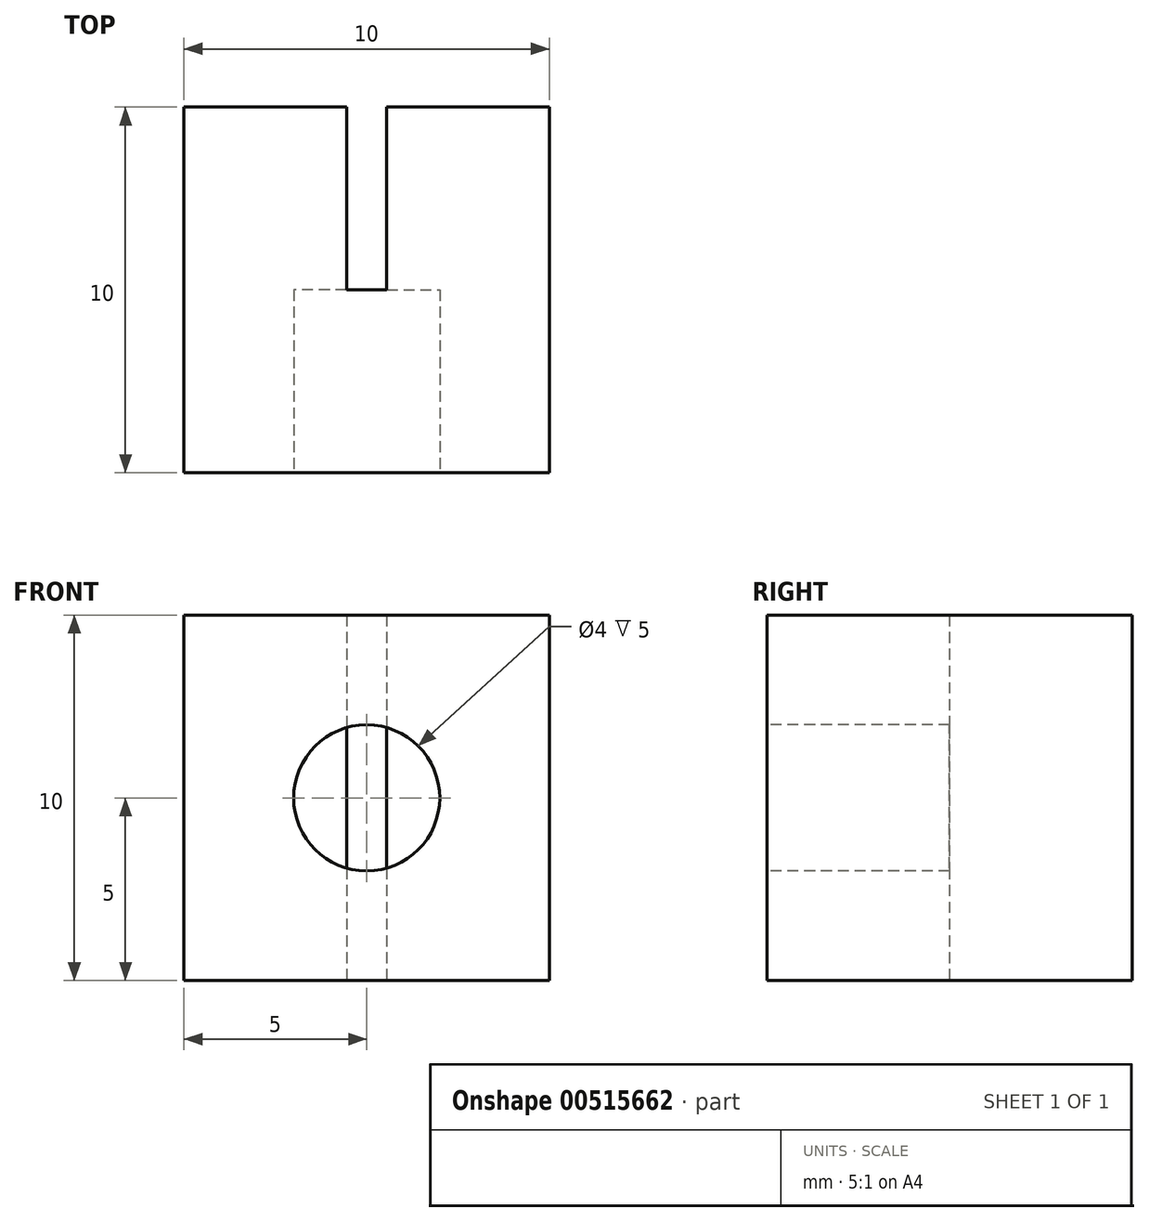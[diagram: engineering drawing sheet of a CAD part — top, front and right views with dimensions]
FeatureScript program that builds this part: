
annotation { "Feature Type Name" : "Feature", "Feature Type Description" : "" }
export const myFeature = defineFeature(function(context is Context, id is Id, definition is map)
    precondition{}
    {
        {
            var Q0;
            Q0=qCreatedBy(makeId("Top.planeOp"),FACE);
            var sketch = newSketch(context, id + "F0", { "sketchPlane" : qUnion([Q0])});
            skLineSegment(sketch, "E0.bottom", {"start": v(5, -5) * mm, "end": v(-5, -5) * mm});
            skLineSegment(sketch, "E0.top", {"start": v(5, 5) * mm, "end": v(0.55, 5) * mm});
            skLineSegment(sketch, "E0.left", {"start": v(5, -5) * mm, "end": v(5, 5) * mm});
            skLineSegment(sketch, "E0.right", {"start": v(-5, -5) * mm, "end": v(-5, 5) * mm});
            skPoint(sketch, "E0.middle", {"position": v(0, 0) * mm});
            skLineSegment(sketch, "E1", {"start": v(-0.55, 5) * mm, "end": v(-0.55, 0) * mm});
            skLineSegment(sketch, "E2.MirrorCS", {"start": v(0.55, 5) * mm, "end": v(0.55, 0) * mm});
            skLineSegment(sketch, "E3", {"start": v(-0.55, 0) * mm, "end": v(0.55, 0) * mm});
            skLineSegment(sketch, "E4.trimOffspring", {"start": v(-0.55, 5) * mm, "end": v(-5, 5) * mm});
            skSolve(sketch);
        }
        {
            var Q0;
            Q0 = qSketchRegion(id + "F0", true);
            extrude(context, id + "F1", {"entities" : qUnion([Q0]), "depth" : 10 * mm, "offsetDistance" : 25 * mm});
        }
        {
            var Q0;
            Q0=makeQuery(id+"F1.opExtrude","SWEPT_FACE",FACE,{"disambiguationData":[OSD([sQuery(id+"F0.wireOp",EDGE,"E0.bottom")])]});
            var sketch = newSketch(context, id + "F2", { "sketchPlane" : qUnion([Q0])});
            skCircle(sketch, "E5", {"center": v(0, 5) * mm, "radius": 2 * mm});
            skPoint(sketch, "E5.centerSnap0", {"position": v(-5, 5) * mm});
            skPoint(sketch, "E5.centerSnap1", {"position": v(0, 0) * mm});
            skSolve(sketch);
        }
        {
            var Q0;
            Q0 = qSketchRegion(id + "F2", true);
            extrude(context, id + "F3", {"entities" : qUnion([Q0]), "operationType" : NewBodyOperationType.REMOVE, "oppositeDirection" : true, "depth" : 5 * mm, "offsetDistance" : 25 * mm});
        }
    });
